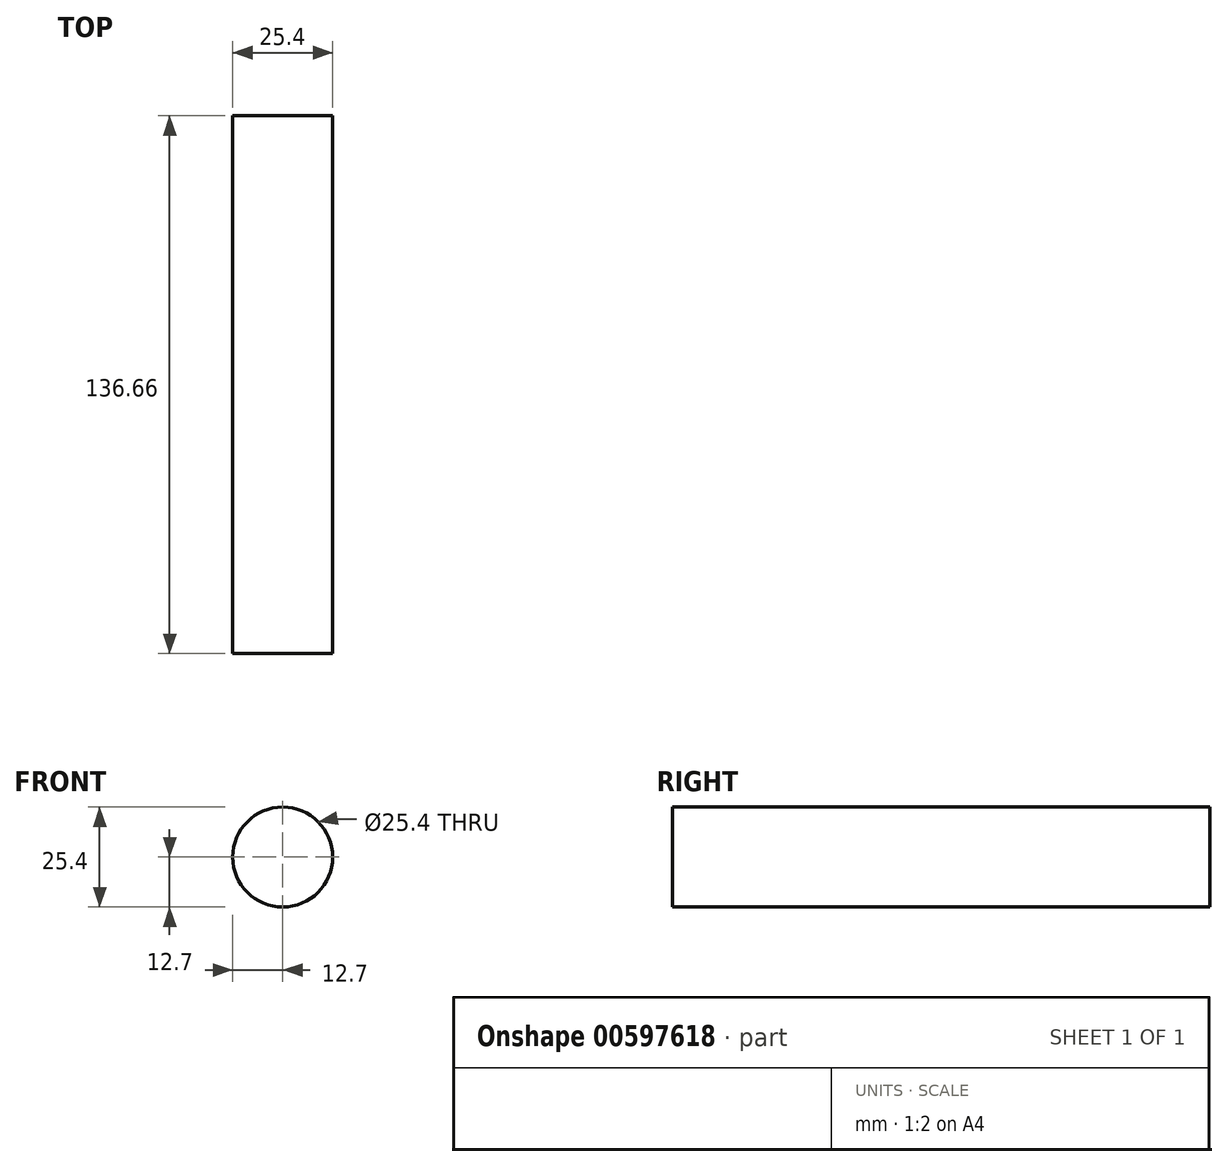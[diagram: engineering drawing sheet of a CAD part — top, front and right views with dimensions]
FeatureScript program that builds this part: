
annotation { "Feature Type Name" : "Feature", "Feature Type Description" : "" }
export const myFeature = defineFeature(function(context is Context, id is Id, definition is map)
    precondition{}
    {
        {
            var Q0;
            Q0=qCreatedBy(makeId("Front.planeOp"),FACE);
            var sketch = newSketch(context, id + "F0", { "sketchPlane" : qUnion([Q0])});
            skCircle(sketch, "E0", {"center": v(0, 0) * mm, "radius": 12.7 * mm});
            skSolve(sketch);
        }
        {
            var Q0;
            Q0=sQuery(id+"F0.wireOp",EDGE,"E0");
            extrude(context, id + "F1", {"bodyType" : ToolBodyType.SURFACE, "surfaceEntities" : qUnion([Q0]), "endBound" : BoundingType.SYMMETRIC, "oppositeDirection" : true, "depth" : 136.65 * mm, "offsetDistance" : 25.4 * mm});
        }
    });
